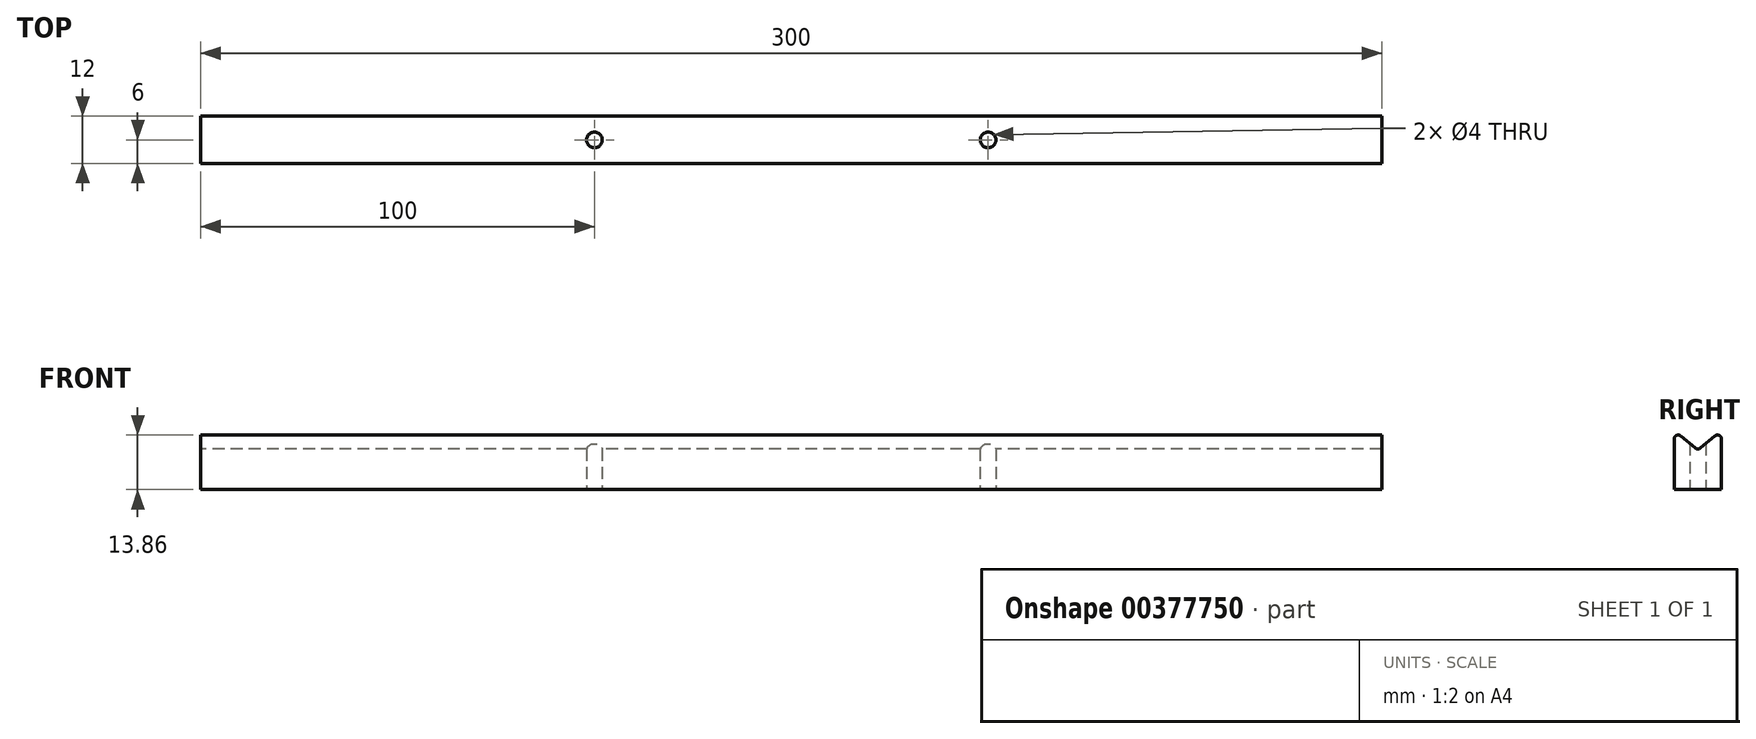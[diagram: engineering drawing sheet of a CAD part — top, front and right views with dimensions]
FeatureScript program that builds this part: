
annotation { "Feature Type Name" : "Feature", "Feature Type Description" : "" }
export const myFeature = defineFeature(function(context is Context, id is Id, definition is map)
    precondition{}
    {
        {
            var Q0;
            Q0=qCreatedBy(makeId("Top.planeOp"),FACE);
            var sketch = newSketch(context, id + "F0", { "sketchPlane" : qUnion([Q0])});
            skLineSegment(sketch, "E0.bottom", {"start": v(150, -6) * mm, "end": v(-150, -6) * mm});
            skLineSegment(sketch, "E0.top", {"start": v(150, 6) * mm, "end": v(-150, 6) * mm});
            skLineSegment(sketch, "E0.left", {"start": v(150, -6) * mm, "end": v(150, 6) * mm});
            skLineSegment(sketch, "E0.right", {"start": v(-150, -6) * mm, "end": v(-150, 6) * mm});
            skPoint(sketch, "E0.middle", {"position": v(0, 0) * mm});
            skLineSegment(sketch, "E1", {"start": v(0, 0) * mm, "end": v(50, 0) * mm, "construction": true});
            skCircle(sketch, "E2", {"center": v(50, 0) * mm, "radius": 2 * mm});
            skCircle(sketch, "E3.MirrorC", {"center": v(-50, 0) * mm, "radius": 2 * mm});
            skSolve(sketch);
        }
        {
            var Q0;
            Q0=makeQuery(id+"F0.imprint","IMPRINT",FACE,{"disambiguationData":[TD([[makeQuery(id+"F0.imprint","IMPRINT",EDGE,{"derivedFrom":sQuery(id+"F0.wireOp",EDGE,"E0.bottom")}),-1.0]])]});
            extrude(context, id + "F1", {"entities" : qUnion([Q0]), "depth" : 15 * mm});
        }
        {
            var Q0;
            Q0=makeQuery(id+"F1.opExtrude","SWEPT_FACE",FACE,{"disambiguationData":[OSD([sQuery(id+"F0.wireOp",EDGE,"E0.left")])]});
            var sketch = newSketch(context, id + "F2", { "sketchPlane" : qUnion([Q0])});
            skLineSegment(sketch, "E4", {"start": v(0, 15) * mm, "end": v(0, 10) * mm, "construction": true});
            skPoint(sketch, "E4.endSnap0", {"position": v(0, 15) * mm});
            skLineSegment(sketch, "E5", {"start": v(-6, 15) * mm, "end": v(0, 10) * mm});
            skLineSegment(sketch, "E6", {"start": v(0, 10) * mm, "end": v(6, 15) * mm});
            skSolve(sketch);
        }
        {
            var Q0;
            Q0=makeQuery(id+"F2.imprint","IMPRINT",FACE,{"disambiguationData":[TD([[makeQuery(id+"F2.imprint","IMPRINT",EDGE,{"derivedFrom":sQuery(id+"F2.wireOp",EDGE,"E5")}),1.0]])]});
            extrude(context, id + "F3", {"entities" : qUnion([Q0]), "operationType" : NewBodyOperationType.REMOVE, "endBound" : BoundingType.THROUGH_ALL, "oppositeDirection" : true, "depth" : 25 * mm});
        }
        {
            var Q0;
            {var subQ0=sQuery(id+"F0.wireOp",EDGE,"E0.bottom");Q0=makeQuery(id+"F3.boolean.opBoolean","MERGE",EDGE,{"derivedFrom":[makeQuery(id+"F1.opExtrude","CAP_EDGE",EDGE,{"disambiguationData":[OSD([subQ0])],"isStart":false}),makeQuery(id+"F3.opExtrude","SWEPT_EDGE",EDGE,{"disambiguationData":[OSD([subQ0,sQuery(id+"F0.wireOp",EDGE,"E0.left"),sQuery(id+"F2.wireOp",EDGE,"E5")])]})]});}
            var Q1;
            {var subQ0=sQuery(id+"F0.wireOp",EDGE,"E0.top");Q1=makeQuery(id+"F3.boolean.opBoolean","MERGE",EDGE,{"derivedFrom":[makeQuery(id+"F1.opExtrude","CAP_EDGE",EDGE,{"disambiguationData":[OSD([subQ0])],"isStart":false}),makeQuery(id+"F3.opExtrude","SWEPT_EDGE",EDGE,{"disambiguationData":[OSD([subQ0,sQuery(id+"F0.wireOp",EDGE,"E0.left"),sQuery(id+"F2.wireOp",EDGE,"E6")])]})]});}
            var Q2;
            Q2=makeQuery(id+"F3.boolean.opBoolean","COPY",EDGE,{"derivedFrom":makeQuery(id+"F3.opExtrude","SWEPT_EDGE",EDGE,{"disambiguationData":[OSD([sQuery(id+"F2.wireOp",EDGE,"E5"),sQuery(id+"F2.wireOp",EDGE,"E6")])]})});
            fillet(context, id + "F4", {"entities" : qUnion([Q0, Q1, Q2]), "radius" : 1 * mm, "tangentPropagation" : true, "allowEdgeOverflow" : false});
        }
    });
